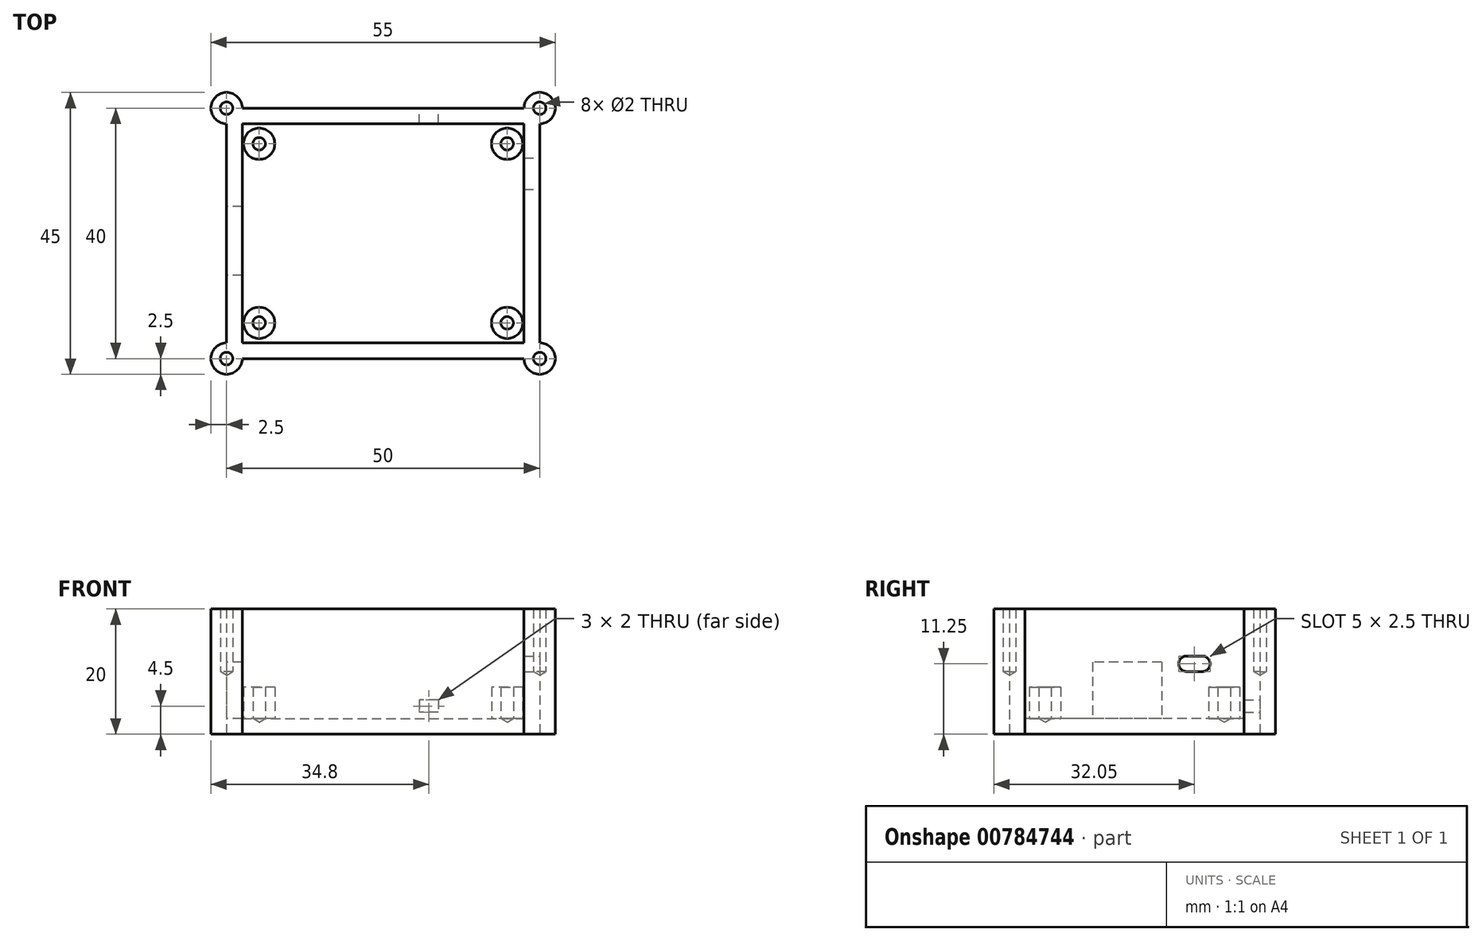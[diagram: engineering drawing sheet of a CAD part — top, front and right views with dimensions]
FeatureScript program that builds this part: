
annotation { "Feature Type Name" : "Feature", "Feature Type Description" : "" }
export const myFeature = defineFeature(function(context is Context, id is Id, definition is map)
    precondition{}
    {
        {
            var Q0;
            Q0=qCreatedBy(makeId("Top.planeOp"),FACE);
            var sketch = newSketch(context, id + "F0", { "sketchPlane" : qUnion([Q0])});
            skLineSegment(sketch, "E0.bottom", {"start": v(-22.5, 17.5) * mm, "end": v(22.5, 17.5) * mm, "construction": true});
            skLineSegment(sketch, "E0.top", {"start": v(-22.5, -17.5) * mm, "end": v(22.5, -17.5) * mm, "construction": true});
            skLineSegment(sketch, "E0.left", {"start": v(-22.5, 17.5) * mm, "end": v(-22.5, -17.5) * mm, "construction": true});
            skLineSegment(sketch, "E0.right", {"start": v(22.5, 17.5) * mm, "end": v(22.5, -17.5) * mm, "construction": true});
            skLineSegment(sketch, "E1.bottom", {"start": v(-25, 20) * mm, "end": v(25, 20) * mm});
            skLineSegment(sketch, "E1.top", {"start": v(-25, -20) * mm, "end": v(25, -20) * mm});
            skLineSegment(sketch, "E1.left", {"start": v(-25, 20) * mm, "end": v(-25, -20) * mm});
            skLineSegment(sketch, "E1.right", {"start": v(25, 20) * mm, "end": v(25, -20) * mm});
            skCircle(sketch, "E2", {"center": v(25, 20) * mm, "radius": 2.5 * mm});
            skCircle(sketch, "E3", {"center": v(-25, 20) * mm, "radius": 2.5 * mm});
            skCircle(sketch, "E4", {"center": v(-25, -20) * mm, "radius": 2.5 * mm});
            skCircle(sketch, "E5", {"center": v(25, -20) * mm, "radius": 2.5 * mm});
            skLineSegment(sketch, "E6.bottom", {"start": v(-19.8, 14.3) * mm, "end": v(19.8, 14.3) * mm, "construction": true});
            skLineSegment(sketch, "E6.top", {"start": v(-19.8, -14.3) * mm, "end": v(19.8, -14.3) * mm, "construction": true});
            skLineSegment(sketch, "E6.left", {"start": v(-19.8, 14.3) * mm, "end": v(-19.8, -14.3) * mm, "construction": true});
            skLineSegment(sketch, "E6.right", {"start": v(19.8, 14.3) * mm, "end": v(19.8, -14.3) * mm, "construction": true});
            skPoint(sketch, "E7", {"position": v(-19.8, 14.3) * mm});
            skPoint(sketch, "E8", {"position": v(19.8, 14.3) * mm});
            skPoint(sketch, "E9", {"position": v(19.8, -14.3) * mm});
            skPoint(sketch, "E10", {"position": v(-19.8, -14.3) * mm});
            skSolve(sketch);
        }
        {
            var Q0;
            Q0 = qSketchRegion(id + "F0", true);
            extrude(context, id + "F1", {"entities" : qUnion([Q0]), "depth" : 20 * mm, "offsetDistance" : 25 * mm});
        }
        {
            var Q0;
            Q0=makeQuery(id+"F1.opExtrude","CAP_FACE",FACE,{"disambiguationData":[OSD([sQuery(id+"F0.wireOp",EDGE,"E1.bottom"),sQuery(id+"F0.wireOp",EDGE,"E1.top"),sQuery(id+"F0.wireOp",EDGE,"E1.left"),sQuery(id+"F0.wireOp",EDGE,"E1.right"),sQuery(id+"F0.wireOp",EDGE,"E2"),sQuery(id+"F0.wireOp",EDGE,"E3"),sQuery(id+"F0.wireOp",EDGE,"E4"),sQuery(id+"F0.wireOp",EDGE,"E5")])],"isStart":false});
            shell(context, id + "F2", {"entities" : qUnion([Q0]), "thickness" : 2.5 * mm});
        }
        {
            var Q0;
            Q0=makeQuery(id+"F2.opShell","OFFSET_FACE",FACE,{"disambiguationData":[OSD([sQuery(id+"F0.wireOp",EDGE,"E1.bottom"),sQuery(id+"F0.wireOp",EDGE,"E1.top"),sQuery(id+"F0.wireOp",EDGE,"E1.left"),sQuery(id+"F0.wireOp",EDGE,"E1.right"),sQuery(id+"F0.wireOp",EDGE,"E2"),sQuery(id+"F0.wireOp",EDGE,"E3"),sQuery(id+"F0.wireOp",EDGE,"E4"),sQuery(id+"F0.wireOp",EDGE,"E5")])]});
            var sketch = newSketch(context, id + "F3", { "sketchPlane" : qUnion([Q0])});
            skCircle(sketch, "E11", {"center": v(-19.8, 14.3) * mm, "radius": 2.5 * mm});
            skCircle(sketch, "E12", {"center": v(19.8, 14.3) * mm, "radius": 2.5 * mm});
            skCircle(sketch, "E13", {"center": v(-19.8, -14.3) * mm, "radius": 2.5 * mm});
            skCircle(sketch, "E14", {"center": v(19.8, -14.3) * mm, "radius": 2.5 * mm});
            skSolve(sketch);
        }
        {
            var Q0;
            Q0 = qSketchRegion(id + "F3", true);
            extrude(context, id + "F4", {"entities" : qUnion([Q0]), "operationType" : NewBodyOperationType.ADD, "depth" : 5 * mm, "offsetDistance" : 25 * mm});
        }
        {
            var Q0;
            Q0=makeQuery(id+"F4.opExtrude","CAP_FACE",FACE,{"disambiguationData":[OSD([sQuery(id+"F3.wireOp",EDGE,"E11")])],"isStart":false});
            var sketch = newSketch(context, id + "F5", { "sketchPlane" : qUnion([Q0])});
            skPoint(sketch, "E15", {"position": v(-19.8, 14.3) * mm});
            skSolve(sketch);
        }
        {
            var Q0;
            Q0=makeQuery(id+"F4.opExtrude","CAP_FACE",FACE,{"disambiguationData":[OSD([sQuery(id+"F3.wireOp",EDGE,"E13")])],"isStart":false});
            var sketch = newSketch(context, id + "F6", { "sketchPlane" : qUnion([Q0])});
            skPoint(sketch, "E16", {"position": v(-19.8, -14.3) * mm});
            skSolve(sketch);
        }
        {
            var Q0;
            Q0=makeQuery(id+"F4.opExtrude","CAP_FACE",FACE,{"disambiguationData":[OSD([sQuery(id+"F3.wireOp",EDGE,"E12")])],"isStart":false});
            var sketch = newSketch(context, id + "F7", { "sketchPlane" : qUnion([Q0])});
            skPoint(sketch, "E17", {"position": v(19.8, 14.3) * mm});
            skSolve(sketch);
        }
        {
            var Q0;
            Q0=makeQuery(id+"F4.opExtrude","CAP_FACE",FACE,{"disambiguationData":[OSD([sQuery(id+"F3.wireOp",EDGE,"E14")])],"isStart":false});
            var sketch = newSketch(context, id + "F8", { "sketchPlane" : qUnion([Q0])});
            skPoint(sketch, "E18", {"position": v(19.8, -14.3) * mm});
            skSolve(sketch);
        }
        {
            var Q0;
            Q0=makeQuery(id+"F1.opExtrude","CAP_FACE",FACE,{"disambiguationData":[OSD([sQuery(id+"F0.wireOp",EDGE,"E1.bottom"),sQuery(id+"F0.wireOp",EDGE,"E1.top"),sQuery(id+"F0.wireOp",EDGE,"E1.left"),sQuery(id+"F0.wireOp",EDGE,"E1.right"),sQuery(id+"F0.wireOp",EDGE,"E2"),sQuery(id+"F0.wireOp",EDGE,"E3"),sQuery(id+"F0.wireOp",EDGE,"E4"),sQuery(id+"F0.wireOp",EDGE,"E5")])],"isStart":false});
            var sketch = newSketch(context, id + "F9", { "sketchPlane" : qUnion([Q0])});
            skPoint(sketch, "E19", {"position": v(-25, 20) * mm});
            skPoint(sketch, "E20", {"position": v(25, 20) * mm});
            skPoint(sketch, "E21", {"position": v(25, -20) * mm});
            skPoint(sketch, "E22", {"position": v(-25, -20) * mm});
            skSolve(sketch);
        }
        {
            var Q0;
            Q0=makeQuery(id+"F1.opExtrude","SWEPT_FACE",FACE,{"disambiguationData":[OSD([sQuery(id+"F0.wireOp",EDGE,"E1.right")])]});
            var sketch = newSketch(context, id + "F10", { "sketchPlane" : qUnion([Q0])});
            skLineSegment(sketch, "E23.bottom", {"start": v(8.3, 12.5) * mm, "end": v(10.8, 12.5) * mm});
            skArc(sketch, "E24", {"start": v(10.8, 10) * mm, "mid": v(12.05, 11.25) * mm, "end": v(10.8, 12.5) * mm});
            skLineSegment(sketch, "E25", {"start": v(10.8, 10) * mm, "end": v(8.3, 10) * mm});
            skArc(sketch, "E26", {"start": v(8.3, 12.5) * mm, "mid": v(7.05, 11.25) * mm, "end": v(8.3, 10) * mm});
            skSolve(sketch);
        }
        {
            var Q0;
            Q0=makeQuery(id+"F1.opExtrude","SWEPT_FACE",FACE,{"disambiguationData":[OSD([sQuery(id+"F0.wireOp",EDGE,"E1.bottom")])]});
            var sketch = newSketch(context, id + "F11", { "sketchPlane" : qUnion([Q0])});
            skLineSegment(sketch, "E27.bottom", {"start": v(-8.8, 5.5) * mm, "end": v(-5.8, 5.5) * mm});
            skLineSegment(sketch, "E27.top", {"start": v(-8.8, 3.5) * mm, "end": v(-5.8, 3.5) * mm});
            skLineSegment(sketch, "E27.left", {"start": v(-8.8, 5.5) * mm, "end": v(-8.8, 3.5) * mm});
            skLineSegment(sketch, "E27.right", {"start": v(-5.8, 5.5) * mm, "end": v(-5.8, 3.5) * mm});
            skSolve(sketch);
        }
        {
            var Q0;
            Q0 = qSketchRegion(id + "F11", true);
            extrude(context, id + "F12", {"entities" : qUnion([Q0]), "operationType" : NewBodyOperationType.REMOVE, "oppositeDirection" : true, "depth" : 5 * mm, "offsetDistance" : 25 * mm});
        }
        {
            var Q0;
            Q0=makeQuery(id+"F10.imprint","IMPRINT",FACE,{"disambiguationData":[TD([[makeQuery(id+"F10.imprint","IMPRINT",EDGE,{"derivedFrom":sQuery(id+"F10.wireOp",EDGE,"E23.bottom")}),-1.0]])]});
            var Q1;
            Q1=sQuery(id+"F10.wireOp",EDGE,"E26");
            var Q2;
            Q2=sQuery(id+"F10.wireOp",EDGE,"E24");
            var Q3;
            Q3=sQuery(id+"F10.wireOp",EDGE,"E23.bottom");
            var Q4;
            Q4=sQuery(id+"F10.wireOp",EDGE,"E25");
            extrude(context, id + "F13", {"entities" : qUnion([Q0]), "operationType" : NewBodyOperationType.REMOVE, "surfaceEntities" : qUnion([Q1, Q2, Q3, Q4]), "oppositeDirection" : true, "depth" : 5 * mm, "offsetDistance" : 25 * mm});
        }
        {
            var Q0;
            Q0=makeQuery(id+"F1.opExtrude","SWEPT_FACE",FACE,{"disambiguationData":[OSD([sQuery(id+"F0.wireOp",EDGE,"E1.left")])]});
            var sketch = newSketch(context, id + "F14", { "sketchPlane" : qUnion([Q0])});
            skLineSegment(sketch, "E28.bottom", {"start": v(-4.3, 11.5) * mm, "end": v(6.7, 11.5) * mm});
            skLineSegment(sketch, "E28.top", {"start": v(-4.3, 2.5) * mm, "end": v(6.7, 2.5) * mm});
            skLineSegment(sketch, "E28.left", {"start": v(-4.3, 11.5) * mm, "end": v(-4.3, 2.5) * mm});
            skLineSegment(sketch, "E28.right", {"start": v(6.7, 11.5) * mm, "end": v(6.7, 2.5) * mm});
            skSolve(sketch);
        }
        {
            var Q0;
            Q0 = qSketchRegion(id + "F14", true);
            extrude(context, id + "F15", {"entities" : qUnion([Q0]), "operationType" : NewBodyOperationType.REMOVE, "oppositeDirection" : true, "depth" : 5 * mm, "offsetDistance" : 25 * mm});
        }
        {
            var Q0;
            Q0=sQuery(id+"F9.wireOp",VERTEX,"E19");
            var Q1;
            Q1=sQuery(id+"F9.wireOp",VERTEX,"E20");
            var Q2;
            Q2=sQuery(id+"F9.wireOp",VERTEX,"E22");
            var Q3;
            Q3=sQuery(id+"F9.wireOp",VERTEX,"E21");
            var Q4;
            Q4=makeQuery(id+"F1.opExtrude","SWEPT_BODY",BODY,{"disambiguationData":[OSD([sQuery(id+"F0.wireOp",EDGE,"E1.bottom"),sQuery(id+"F0.wireOp",EDGE,"E1.top"),sQuery(id+"F0.wireOp",EDGE,"E1.left"),sQuery(id+"F0.wireOp",EDGE,"E1.right"),sQuery(id+"F0.wireOp",EDGE,"E2"),sQuery(id+"F0.wireOp",EDGE,"E3"),sQuery(id+"F0.wireOp",EDGE,"E4"),sQuery(id+"F0.wireOp",EDGE,"E5")])]});
            hole(context, id + "F16", {"style" : HoleStyle.SIMPLE, "endStyle" : HoleEndStyle.BLIND, "holeDiameter" : 2 * mm, "majorDiameter" : 5 * mm, "holeDepth" : 10 * mm, "isTappedThrough" : true, "tappedDepth" : 12 * mm, "tapClearance" : 3, "locations" : qUnion([Q0, Q1, Q2, Q3]), "scope" : qUnion([Q4]), "startStyle" : HoleStartStyle.SKETCH});
        }
        {
            var Q0;
            Q0=sQuery(id+"F5.wireOp",VERTEX,"E15");
            var Q1;
            Q1=sQuery(id+"F7.wireOp",VERTEX,"E17");
            var Q2;
            Q2=sQuery(id+"F6.wireOp",VERTEX,"E16");
            var Q3;
            Q3=sQuery(id+"F8.wireOp",VERTEX,"E18");
            var Q4;
            Q4=makeQuery(id+"F1.opExtrude","SWEPT_BODY",BODY,{"disambiguationData":[OSD([sQuery(id+"F0.wireOp",EDGE,"E1.bottom"),sQuery(id+"F0.wireOp",EDGE,"E1.top"),sQuery(id+"F0.wireOp",EDGE,"E1.left"),sQuery(id+"F0.wireOp",EDGE,"E1.right"),sQuery(id+"F0.wireOp",EDGE,"E2"),sQuery(id+"F0.wireOp",EDGE,"E3"),sQuery(id+"F0.wireOp",EDGE,"E4"),sQuery(id+"F0.wireOp",EDGE,"E5")])]});
            hole(context, id + "F17", {"style" : HoleStyle.SIMPLE, "endStyle" : HoleEndStyle.BLIND, "holeDiameter" : 2 * mm, "majorDiameter" : 5 * mm, "holeDepth" : 5 * mm, "isTappedThrough" : true, "tappedDepth" : 12 * mm, "tapClearance" : 3, "locations" : qUnion([Q0, Q1, Q2, Q3]), "scope" : qUnion([Q4]), "startStyle" : HoleStartStyle.SKETCH});
        }
    });
